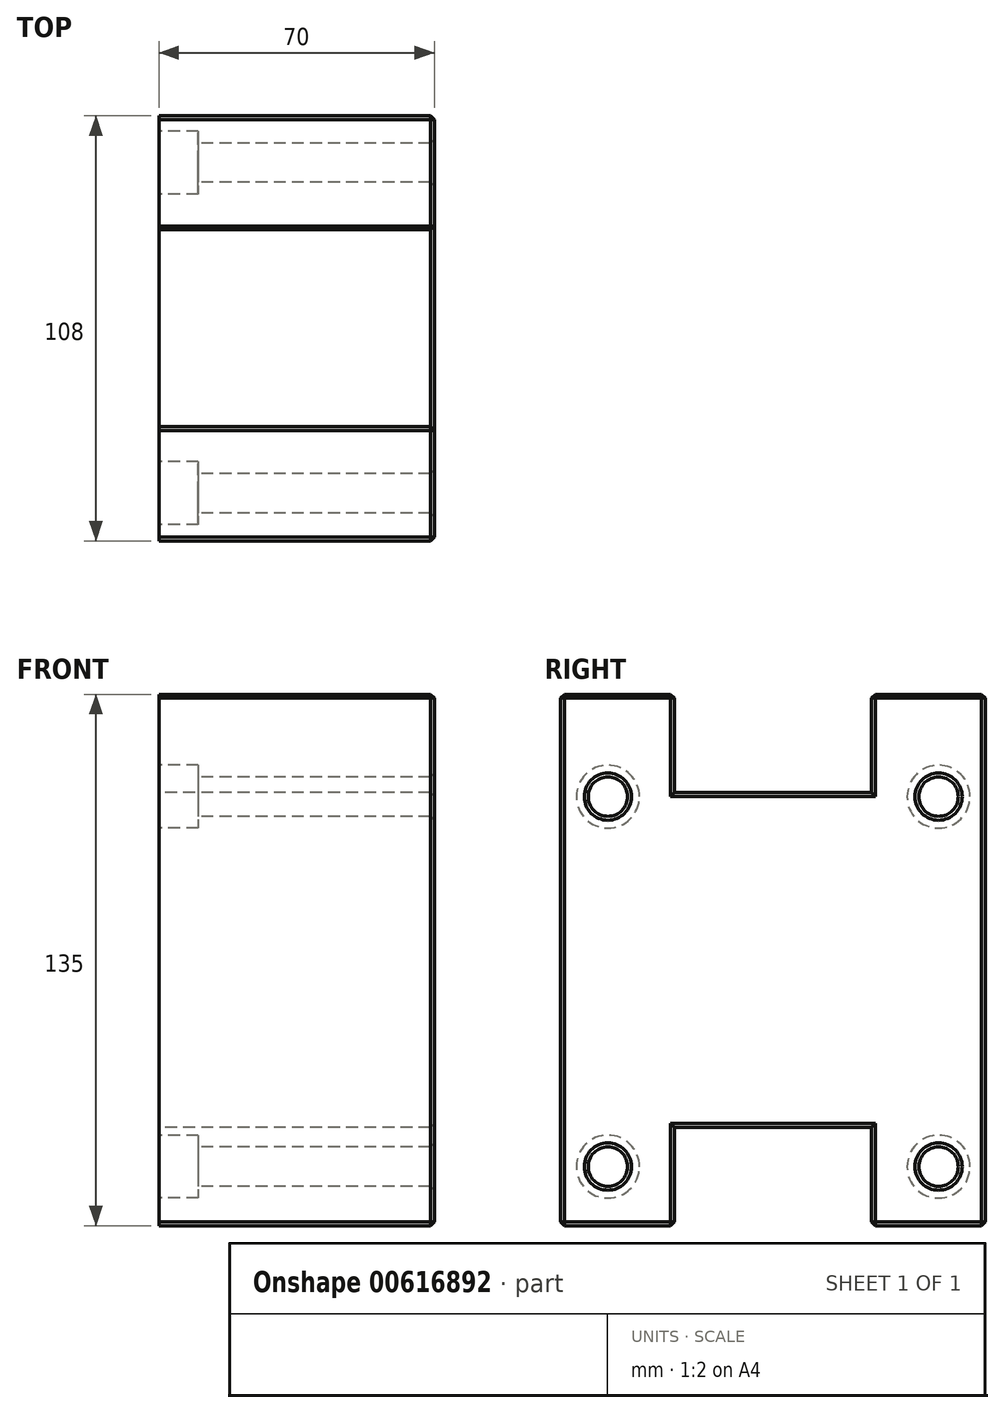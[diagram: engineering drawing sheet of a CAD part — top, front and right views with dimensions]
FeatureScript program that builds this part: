
annotation { "Feature Type Name" : "Feature", "Feature Type Description" : "" }
export const myFeature = defineFeature(function(context is Context, id is Id, definition is map)
    precondition{}
    {
        {
            var Q0;
            Q0=qCreatedBy(makeId("Right.planeOp"),FACE);
            var sketch = newSketch(context, id + "F0", { "sketchPlane" : qUnion([Q0])});
            skLineSegment(sketch, "E0.bottom", {"start": v(-54, 67.5) * mm, "end": v(-25, 67.5) * mm});
            skLineSegment(sketch, "E0.top", {"start": v(-54, -67.5) * mm, "end": v(-25, -67.5) * mm});
            skLineSegment(sketch, "E0.left", {"start": v(-54, 67.5) * mm, "end": v(-54, -67.5) * mm});
            skLineSegment(sketch, "E0.right", {"start": v(54, 67.5) * mm, "end": v(54, -67.5) * mm});
            skPoint(sketch, "E0.middle", {"position": v(0, 0) * mm});
            skLineSegment(sketch, "E1", {"start": v(-25, 67.5) * mm, "end": v(-25, 42.5) * mm});
            skLineSegment(sketch, "E2", {"start": v(-25, 42.5) * mm, "end": v(25, 42.5) * mm});
            skLineSegment(sketch, "E3", {"start": v(25, 42.5) * mm, "end": v(25, 67.5) * mm});
            skLineSegment(sketch, "E4", {"start": v(-25, -67.5) * mm, "end": v(-25, -42.5) * mm});
            skLineSegment(sketch, "E5", {"start": v(-25, -42.5) * mm, "end": v(25, -42.5) * mm});
            skLineSegment(sketch, "E6", {"start": v(25, -42.5) * mm, "end": v(25, -67.5) * mm});
            skLineSegment(sketch, "E7.trimOffspring", {"start": v(25, 67.5) * mm, "end": v(54, 67.5) * mm});
            skLineSegment(sketch, "E8.trimOffspring", {"start": v(25, -67.5) * mm, "end": v(54, -67.5) * mm});
            skSolve(sketch);
        }
        {
            var Q0;
            Q0=makeQuery(id+"F0.imprint","IMPRINT",FACE,{"disambiguationData":[TD([[makeQuery(id+"F0.imprint","IMPRINT",EDGE,{"derivedFrom":sQuery(id+"F0.wireOp",EDGE,"ETDeel4q-IsmD-NWzm-VhFC-4y5bX9WcGCPe")}),-1.0]])]});
            var Q1;
            Q1=makeQuery(id+"F0.imprint","IMPRINT",FACE,{"disambiguationData":[TD([[makeQuery(id+"F0.imprint","IMPRINT",EDGE,{"derivedFrom":sQuery(id+"F0.wireOp",EDGE,"E0.bottom")}),-1.0]])]});
            extrude(context, id + "F1", {"entities" : qUnion([Q0, Q1]), "depth" : 70 * mm, "offsetDistance" : 25 * mm});
        }
        {
            var Q0;
            Q0=makeQuery(id+"F1.opExtrude","CAP_FACE",FACE,{"disambiguationData":[OSD([sQuery(id+"F0.wireOp",EDGE,"E0.bottom"),sQuery(id+"F0.wireOp",EDGE,"E0.top"),sQuery(id+"F0.wireOp",EDGE,"E0.left"),sQuery(id+"F0.wireOp",EDGE,"E0.right"),sQuery(id+"F0.wireOp",EDGE,"E1"),sQuery(id+"F0.wireOp",EDGE,"E2"),sQuery(id+"F0.wireOp",EDGE,"E3"),sQuery(id+"F0.wireOp",EDGE,"E4"),sQuery(id+"F0.wireOp",EDGE,"E5"),sQuery(id+"F0.wireOp",EDGE,"E6"),sQuery(id+"F0.wireOp",EDGE,"E7.trimOffspring"),sQuery(id+"F0.wireOp",EDGE,"E8.trimOffspring")])],"isStart":true});
            var sketch = newSketch(context, id + "F2", { "sketchPlane" : qUnion([Q0])});
            skCircle(sketch, "E9", {"center": v(41.92, 41.5) * mm, "radius": 8 * mm});
            skCircle(sketch, "E10", {"center": v(-42.08, 41.5) * mm, "radius": 8 * mm});
            skCircle(sketch, "E11", {"center": v(41.92, -52.5) * mm, "radius": 8 * mm});
            skCircle(sketch, "E12", {"center": v(-42.08, -52.5) * mm, "radius": 8 * mm});
            skLineSegment(sketch, "E13", {"start": v(41.92, 41.5) * mm, "end": v(41.92, -52.5) * mm, "construction": true});
            skLineSegment(sketch, "E14", {"start": v(41.92, 41.5) * mm, "end": v(-42.08, 41.5) * mm, "construction": true});
            skLineSegment(sketch, "E15", {"start": v(-42.08, 41.5) * mm, "end": v(-42.08, -52.5) * mm, "construction": true});
            skLineSegment(sketch, "E16", {"start": v(41.92, -52.5) * mm, "end": v(-368.86, -52.5) * mm, "construction": true});
            skSolve(sketch);
        }
        {
            var Q0;
            Q0 = qSketchRegion(id + "F2", true);
            extrude(context, id + "F3", {"entities" : qUnion([Q0]), "operationType" : NewBodyOperationType.REMOVE, "oppositeDirection" : true, "depth" : 10 * mm, "offsetDistance" : 25 * mm});
        }
        {
            var Q0;
            Q0=makeQuery(id+"F1.opExtrude","CAP_FACE",FACE,{"disambiguationData":[OSD([sQuery(id+"F0.wireOp",EDGE,"E0.bottom"),sQuery(id+"F0.wireOp",EDGE,"E0.top"),sQuery(id+"F0.wireOp",EDGE,"E0.left"),sQuery(id+"F0.wireOp",EDGE,"E0.right"),sQuery(id+"F0.wireOp",EDGE,"E1"),sQuery(id+"F0.wireOp",EDGE,"E2"),sQuery(id+"F0.wireOp",EDGE,"E3"),sQuery(id+"F0.wireOp",EDGE,"E4"),sQuery(id+"F0.wireOp",EDGE,"E5"),sQuery(id+"F0.wireOp",EDGE,"E6"),sQuery(id+"F0.wireOp",EDGE,"E7.trimOffspring"),sQuery(id+"F0.wireOp",EDGE,"E8.trimOffspring")])],"isStart":true});
            var sketch = newSketch(context, id + "F4", { "sketchPlane" : qUnion([Q0])});
            skCircle(sketch, "E17", {"center": v(-42.08, 41.5) * mm, "radius": 5 * mm});
            skCircle(sketch, "E18", {"center": v(41.92, 41.5) * mm, "radius": 5 * mm});
            skCircle(sketch, "E19", {"center": v(41.92, -52.5) * mm, "radius": 5 * mm});
            skCircle(sketch, "E20", {"center": v(-42.08, -52.5) * mm, "radius": 5 * mm});
            skSolve(sketch);
        }
        {
            var Q0;
            Q0 = qSketchRegion(id + "F4", true);
            extrude(context, id + "F5", {"entities" : qUnion([Q0]), "operationType" : NewBodyOperationType.REMOVE, "endBound" : BoundingType.THROUGH_ALL, "oppositeDirection" : true, "depth" : 25 * mm, "offsetDistance" : 25 * mm});
        }
        {
            var Q0;
            Q0=makeQuery(id+"F1.opExtrude","CAP_FACE",FACE,{"disambiguationData":[OSD([sQuery(id+"F0.wireOp",EDGE,"E0.bottom"),sQuery(id+"F0.wireOp",EDGE,"E0.top"),sQuery(id+"F0.wireOp",EDGE,"E0.left"),sQuery(id+"F0.wireOp",EDGE,"E0.right"),sQuery(id+"F0.wireOp",EDGE,"E1"),sQuery(id+"F0.wireOp",EDGE,"E2"),sQuery(id+"F0.wireOp",EDGE,"E3"),sQuery(id+"F0.wireOp",EDGE,"E4"),sQuery(id+"F0.wireOp",EDGE,"E5"),sQuery(id+"F0.wireOp",EDGE,"E6"),sQuery(id+"F0.wireOp",EDGE,"E7.trimOffspring"),sQuery(id+"F0.wireOp",EDGE,"E8.trimOffspring")])],"isStart":false});
            var Q1;
            Q1=makeQuery(id+"F1.opExtrude","SWEPT_EDGE",EDGE,{"disambiguationData":[OSD([sQuery(id+"F0.wireOp",EDGE,"E0.top"),sQuery(id+"F0.wireOp",EDGE,"E0.left")])]});
            var Q2;
            Q2=makeQuery(id+"F1.opExtrude","SWEPT_EDGE",EDGE,{"disambiguationData":[OSD([sQuery(id+"F0.wireOp",EDGE,"E0.top"),sQuery(id+"F0.wireOp",EDGE,"E4")])]});
            var Q3;
            Q3=makeQuery(id+"F1.opExtrude","SWEPT_EDGE",EDGE,{"disambiguationData":[OSD([sQuery(id+"F0.wireOp",EDGE,"E6"),sQuery(id+"F0.wireOp",EDGE,"E8.trimOffspring")])]});
            var Q4;
            Q4=makeQuery(id+"F1.opExtrude","SWEPT_EDGE",EDGE,{"disambiguationData":[OSD([sQuery(id+"F0.wireOp",EDGE,"E0.right"),sQuery(id+"F0.wireOp",EDGE,"E8.trimOffspring")])]});
            var Q5;
            Q5=makeQuery(id+"F1.opExtrude","SWEPT_EDGE",EDGE,{"disambiguationData":[OSD([sQuery(id+"F0.wireOp",EDGE,"E0.bottom"),sQuery(id+"F0.wireOp",EDGE,"E0.left")])]});
            var Q6;
            Q6=makeQuery(id+"F1.opExtrude","SWEPT_EDGE",EDGE,{"disambiguationData":[OSD([sQuery(id+"F0.wireOp",EDGE,"E0.bottom"),sQuery(id+"F0.wireOp",EDGE,"E1")])]});
            var Q7;
            Q7=makeQuery(id+"F1.opExtrude","SWEPT_EDGE",EDGE,{"disambiguationData":[OSD([sQuery(id+"F0.wireOp",EDGE,"E3"),sQuery(id+"F0.wireOp",EDGE,"E7.trimOffspring")])]});
            var Q8;
            Q8=makeQuery(id+"F1.opExtrude","SWEPT_EDGE",EDGE,{"disambiguationData":[OSD([sQuery(id+"F0.wireOp",EDGE,"E0.right"),sQuery(id+"F0.wireOp",EDGE,"E7.trimOffspring")])]});
            chamfer(context, id + "F6", {"entities" : qUnion([Q0, Q1, Q2, Q3, Q4, Q5, Q6, Q7, Q8]), "width" : 1 * mm, "tangentPropagation" : true});
        }
    });
